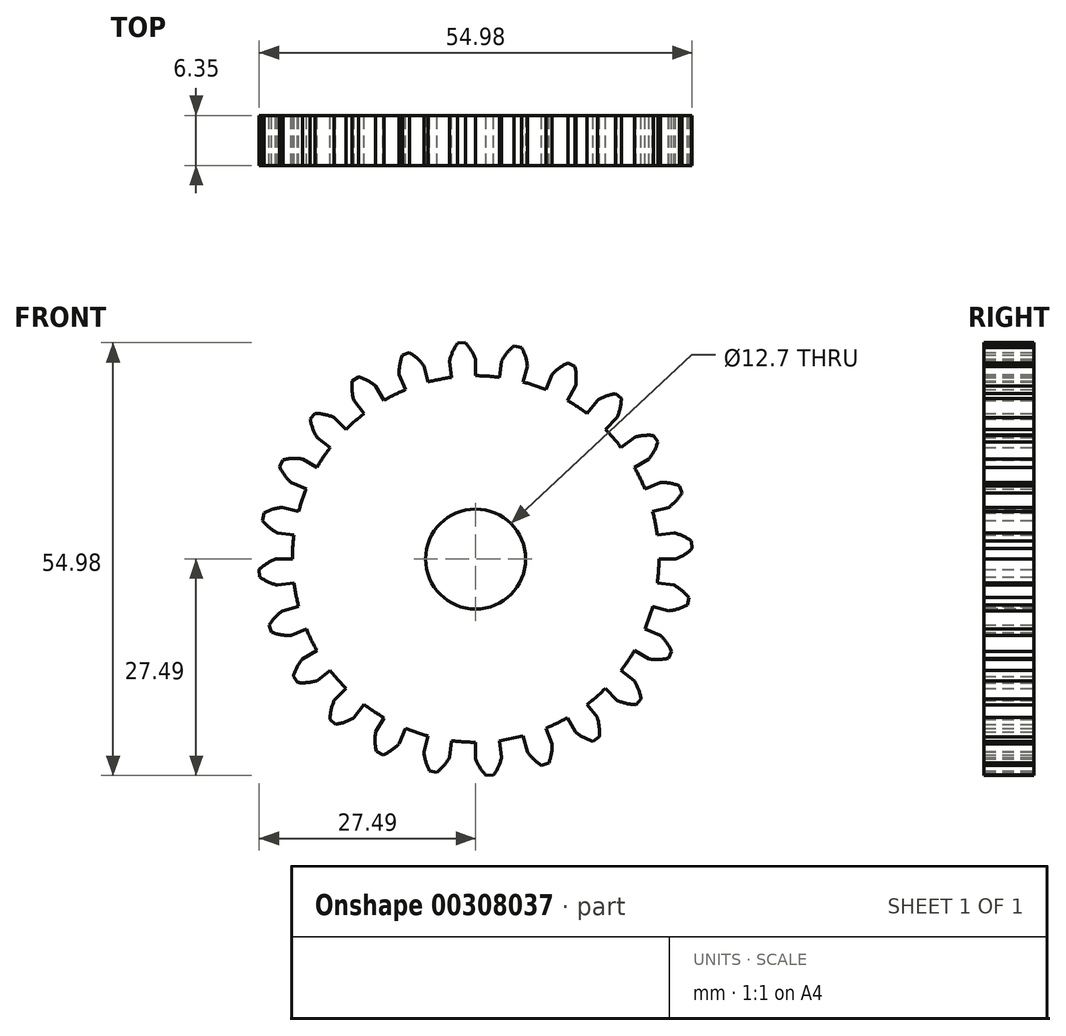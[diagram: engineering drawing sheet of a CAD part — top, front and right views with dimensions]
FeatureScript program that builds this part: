
annotation { "Feature Type Name" : "Feature", "Feature Type Description" : "" }
export const myFeature = defineFeature(function(context is Context, id is Id, definition is map)
    precondition{}
    {
        {
            var Q0;
            Q0=qCreatedBy(makeId("Front.planeOp"),FACE);
            var sketch = newSketch(context, id + "F0", { "sketchPlane" : qUnion([Q0])});
            skArc(sketch, "E0", {"start": v(-3.04, 23.08) * mm, "mid": v(-4.54, 22.83) * mm, "end": v(-6.03, 22.49) * mm});
            skLineSegment(sketch, "E1", {"start": v(0, 23.28) * mm, "end": v(0, 25.4) * mm});
            skArc(sketch, "E2.trimOffspring", {"start": v(0, 25.4) * mm, "mid": v(-0.56, 26.5) * mm, "end": v(-1.32, 27.49) * mm});
            skPoint(sketch, "E3.trimOffspring.end.orphan", {"position": v(0, 47.4) * mm});
            skLineSegment(sketch, "E4", {"start": v(-1.32, 27.49) * mm, "end": v(-1.8, 27.46) * mm});
            skLineSegment(sketch, "E5.MirrorCS", {"start": v(-2.28, 27.43) * mm, "end": v(-1.8, 27.46) * mm});
            skArc(sketch, "E6.MirrorCS", {"start": v(-3.32, 25.18) * mm, "mid": v(-2.9, 26.36) * mm, "end": v(-2.28, 27.43) * mm});
            skLineSegment(sketch, "E7.MirrorCS", {"start": v(-3.04, 23.08) * mm, "end": v(-3.32, 25.18) * mm});
            skLineSegment(sketch, "E8.1.0", {"start": v(-8.9, 21.5) * mm, "end": v(-9.72, 23.47) * mm});
            skArc(sketch, "E8.1.1", {"start": v(-9.72, 23.47) * mm, "mid": v(-9.63, 24.7) * mm, "end": v(-9.3, 25.9) * mm});
            skLineSegment(sketch, "E8.1.2", {"start": v(-9.3, 25.9) * mm, "end": v(-8.84, 26.06) * mm});
            skLineSegment(sketch, "E8.1.3", {"start": v(-8.39, 26.21) * mm, "end": v(-8.84, 26.06) * mm});
            skArc(sketch, "E8.1.4", {"start": v(-6.57, 24.53) * mm, "mid": v(-7.4, 25.46) * mm, "end": v(-8.39, 26.21) * mm});
            skLineSegment(sketch, "E8.1.5", {"start": v(-6.03, 22.49) * mm, "end": v(-6.57, 24.53) * mm});
            skLineSegment(sketch, "E8.2.0", {"start": v(-14.17, 18.47) * mm, "end": v(-15.46, 20.15) * mm});
            skArc(sketch, "E8.2.1", {"start": v(-15.46, 20.15) * mm, "mid": v(-15.7, 21.37) * mm, "end": v(-15.69, 22.61) * mm});
            skLineSegment(sketch, "E8.2.2", {"start": v(-15.69, 22.61) * mm, "end": v(-15.29, 22.88) * mm});
            skLineSegment(sketch, "E8.2.3", {"start": v(-14.89, 23.15) * mm, "end": v(-15.29, 22.88) * mm});
            skArc(sketch, "E8.2.4", {"start": v(-12.7, 22) * mm, "mid": v(-13.74, 22.68) * mm, "end": v(-14.89, 23.15) * mm});
            skLineSegment(sketch, "E8.2.5", {"start": v(-11.64, 20.16) * mm, "end": v(-12.7, 22) * mm});
            skLineSegment(sketch, "E8.3.0", {"start": v(-18.47, 14.17) * mm, "end": v(-20.15, 15.46) * mm});
            skArc(sketch, "E8.3.1", {"start": v(-20.15, 15.46) * mm, "mid": v(-20.7, 16.58) * mm, "end": v(-21, 17.78) * mm});
            skLineSegment(sketch, "E8.3.2", {"start": v(-21, 17.78) * mm, "end": v(-20.69, 18.14) * mm});
            skLineSegment(sketch, "E8.3.3", {"start": v(-20.37, 18.5) * mm, "end": v(-20.69, 18.14) * mm});
            skArc(sketch, "E8.3.4", {"start": v(-17.96, 17.96) * mm, "mid": v(-19.14, 18.35) * mm, "end": v(-20.37, 18.5) * mm});
            skLineSegment(sketch, "E8.3.5", {"start": v(-16.46, 16.46) * mm, "end": v(-17.96, 17.96) * mm});
            skLineSegment(sketch, "E8.4.0", {"start": v(-21.5, 8.9) * mm, "end": v(-23.47, 9.72) * mm});
            skArc(sketch, "E8.4.1", {"start": v(-23.47, 9.72) * mm, "mid": v(-24.28, 10.66) * mm, "end": v(-24.9, 11.74) * mm});
            skLineSegment(sketch, "E8.4.2", {"start": v(-24.9, 11.74) * mm, "end": v(-24.68, 12.17) * mm});
            skLineSegment(sketch, "E8.4.3", {"start": v(-24.47, 12.6) * mm, "end": v(-24.68, 12.17) * mm});
            skArc(sketch, "E8.4.4", {"start": v(-22, 12.7) * mm, "mid": v(-23.24, 12.77) * mm, "end": v(-24.47, 12.6) * mm});
            skLineSegment(sketch, "E8.4.5", {"start": v(-20.16, 11.64) * mm, "end": v(-22, 12.7) * mm});
            skLineSegment(sketch, "E8.5.0", {"start": v(-23.08, 3.04) * mm, "end": v(-25.18, 3.32) * mm});
            skArc(sketch, "E8.5.1", {"start": v(-25.18, 3.32) * mm, "mid": v(-26.2, 4.01) * mm, "end": v(-27.08, 4.9) * mm});
            skLineSegment(sketch, "E8.5.2", {"start": v(-27.08, 4.9) * mm, "end": v(-26.99, 5.37) * mm});
            skLineSegment(sketch, "E8.5.3", {"start": v(-26.9, 5.84) * mm, "end": v(-26.99, 5.37) * mm});
            skArc(sketch, "E8.5.4", {"start": v(-24.53, 6.57) * mm, "mid": v(-25.75, 6.32) * mm, "end": v(-26.9, 5.84) * mm});
            skLineSegment(sketch, "E8.5.5", {"start": v(-22.49, 6.03) * mm, "end": v(-24.53, 6.57) * mm});
            skLineSegment(sketch, "E8.6.0", {"start": v(-23.08, -3.04) * mm, "end": v(-25.18, -3.32) * mm});
            skArc(sketch, "E8.6.1", {"start": v(-25.18, -3.32) * mm, "mid": v(-26.36, -2.9) * mm, "end": v(-27.43, -2.28) * mm});
            skLineSegment(sketch, "E8.6.2", {"start": v(-27.43, -2.28) * mm, "end": v(-27.46, -1.8) * mm});
            skLineSegment(sketch, "E8.6.3", {"start": v(-27.49, -1.32) * mm, "end": v(-27.46, -1.8) * mm});
            skArc(sketch, "E8.6.4", {"start": v(-25.4, 0) * mm, "mid": v(-26.5, -0.56) * mm, "end": v(-27.49, -1.32) * mm});
            skLineSegment(sketch, "E8.6.5", {"start": v(-23.28, 0) * mm, "end": v(-25.4, 0) * mm});
            skLineSegment(sketch, "E8.7.0", {"start": v(-21.5, -8.9) * mm, "end": v(-23.47, -9.72) * mm});
            skArc(sketch, "E8.7.1", {"start": v(-23.47, -9.72) * mm, "mid": v(-24.7, -9.63) * mm, "end": v(-25.9, -9.3) * mm});
            skLineSegment(sketch, "E8.7.2", {"start": v(-25.9, -9.3) * mm, "end": v(-26.06, -8.84) * mm});
            skLineSegment(sketch, "E8.7.3", {"start": v(-26.21, -8.39) * mm, "end": v(-26.06, -8.84) * mm});
            skArc(sketch, "E8.7.4", {"start": v(-24.53, -6.57) * mm, "mid": v(-25.46, -7.4) * mm, "end": v(-26.21, -8.39) * mm});
            skLineSegment(sketch, "E8.7.5", {"start": v(-22.49, -6.03) * mm, "end": v(-24.53, -6.57) * mm});
            skLineSegment(sketch, "E8.8.0", {"start": v(-18.47, -14.17) * mm, "end": v(-20.15, -15.46) * mm});
            skArc(sketch, "E8.8.1", {"start": v(-20.15, -15.46) * mm, "mid": v(-21.37, -15.7) * mm, "end": v(-22.61, -15.69) * mm});
            skLineSegment(sketch, "E8.8.2", {"start": v(-22.61, -15.69) * mm, "end": v(-22.88, -15.29) * mm});
            skLineSegment(sketch, "E8.8.3", {"start": v(-23.15, -14.89) * mm, "end": v(-22.88, -15.29) * mm});
            skArc(sketch, "E8.8.4", {"start": v(-22, -12.7) * mm, "mid": v(-22.68, -13.74) * mm, "end": v(-23.15, -14.89) * mm});
            skLineSegment(sketch, "E8.8.5", {"start": v(-20.16, -11.64) * mm, "end": v(-22, -12.7) * mm});
            skLineSegment(sketch, "E8.9.0", {"start": v(-14.17, -18.47) * mm, "end": v(-15.46, -20.15) * mm});
            skArc(sketch, "E8.9.1", {"start": v(-15.46, -20.15) * mm, "mid": v(-16.58, -20.7) * mm, "end": v(-17.78, -21) * mm});
            skLineSegment(sketch, "E8.9.2", {"start": v(-17.78, -21) * mm, "end": v(-18.14, -20.69) * mm});
            skLineSegment(sketch, "E8.9.3", {"start": v(-18.5, -20.37) * mm, "end": v(-18.14, -20.69) * mm});
            skArc(sketch, "E8.9.4", {"start": v(-17.96, -17.96) * mm, "mid": v(-18.35, -19.14) * mm, "end": v(-18.5, -20.37) * mm});
            skLineSegment(sketch, "E8.9.5", {"start": v(-16.46, -16.46) * mm, "end": v(-17.96, -17.96) * mm});
            skLineSegment(sketch, "E8.10.0", {"start": v(-8.9, -21.5) * mm, "end": v(-9.72, -23.47) * mm});
            skArc(sketch, "E8.10.1", {"start": v(-9.72, -23.47) * mm, "mid": v(-10.66, -24.28) * mm, "end": v(-11.74, -24.9) * mm});
            skLineSegment(sketch, "E8.10.2", {"start": v(-11.74, -24.9) * mm, "end": v(-12.17, -24.68) * mm});
            skLineSegment(sketch, "E8.10.3", {"start": v(-12.6, -24.47) * mm, "end": v(-12.17, -24.68) * mm});
            skArc(sketch, "E8.10.4", {"start": v(-12.7, -22) * mm, "mid": v(-12.77, -23.24) * mm, "end": v(-12.6, -24.47) * mm});
            skLineSegment(sketch, "E8.10.5", {"start": v(-11.64, -20.16) * mm, "end": v(-12.7, -22) * mm});
            skLineSegment(sketch, "E8.11.0", {"start": v(-3.04, -23.08) * mm, "end": v(-3.32, -25.18) * mm});
            skArc(sketch, "E8.11.1", {"start": v(-3.32, -25.18) * mm, "mid": v(-4.01, -26.2) * mm, "end": v(-4.9, -27.08) * mm});
            skLineSegment(sketch, "E8.11.2", {"start": v(-4.9, -27.08) * mm, "end": v(-5.37, -26.99) * mm});
            skLineSegment(sketch, "E8.11.3", {"start": v(-5.84, -26.9) * mm, "end": v(-5.37, -26.99) * mm});
            skArc(sketch, "E8.11.4", {"start": v(-6.57, -24.53) * mm, "mid": v(-6.32, -25.75) * mm, "end": v(-5.84, -26.9) * mm});
            skLineSegment(sketch, "E8.11.5", {"start": v(-6.03, -22.49) * mm, "end": v(-6.57, -24.53) * mm});
            skLineSegment(sketch, "E8.12.0", {"start": v(3.04, -23.08) * mm, "end": v(3.32, -25.18) * mm});
            skArc(sketch, "E8.12.1", {"start": v(3.32, -25.18) * mm, "mid": v(2.9, -26.36) * mm, "end": v(2.28, -27.43) * mm});
            skLineSegment(sketch, "E8.12.2", {"start": v(2.28, -27.43) * mm, "end": v(1.8, -27.46) * mm});
            skLineSegment(sketch, "E8.12.3", {"start": v(1.32, -27.49) * mm, "end": v(1.8, -27.46) * mm});
            skArc(sketch, "E8.12.4", {"start": v(0, -25.4) * mm, "mid": v(0.56, -26.5) * mm, "end": v(1.32, -27.49) * mm});
            skLineSegment(sketch, "E8.12.5", {"start": v(0, -23.28) * mm, "end": v(0, -25.4) * mm});
            skLineSegment(sketch, "E8.13.0", {"start": v(8.9, -21.5) * mm, "end": v(9.72, -23.47) * mm});
            skArc(sketch, "E8.13.1", {"start": v(9.72, -23.47) * mm, "mid": v(9.63, -24.7) * mm, "end": v(9.3, -25.9) * mm});
            skLineSegment(sketch, "E8.13.2", {"start": v(9.3, -25.9) * mm, "end": v(8.84, -26.06) * mm});
            skLineSegment(sketch, "E8.13.3", {"start": v(8.39, -26.21) * mm, "end": v(8.84, -26.06) * mm});
            skArc(sketch, "E8.13.4", {"start": v(6.57, -24.53) * mm, "mid": v(7.4, -25.46) * mm, "end": v(8.39, -26.21) * mm});
            skLineSegment(sketch, "E8.13.5", {"start": v(6.03, -22.49) * mm, "end": v(6.57, -24.53) * mm});
            skLineSegment(sketch, "E8.14.0", {"start": v(14.17, -18.47) * mm, "end": v(15.46, -20.15) * mm});
            skArc(sketch, "E8.14.1", {"start": v(15.46, -20.15) * mm, "mid": v(15.7, -21.37) * mm, "end": v(15.69, -22.61) * mm});
            skLineSegment(sketch, "E8.14.2", {"start": v(15.69, -22.61) * mm, "end": v(15.29, -22.88) * mm});
            skLineSegment(sketch, "E8.14.3", {"start": v(14.89, -23.15) * mm, "end": v(15.29, -22.88) * mm});
            skArc(sketch, "E8.14.4", {"start": v(12.7, -22) * mm, "mid": v(13.74, -22.68) * mm, "end": v(14.89, -23.15) * mm});
            skLineSegment(sketch, "E8.14.5", {"start": v(11.64, -20.16) * mm, "end": v(12.7, -22) * mm});
            skLineSegment(sketch, "E8.15.0", {"start": v(18.47, -14.17) * mm, "end": v(20.15, -15.46) * mm});
            skArc(sketch, "E8.15.1", {"start": v(20.15, -15.46) * mm, "mid": v(20.7, -16.58) * mm, "end": v(21, -17.78) * mm});
            skLineSegment(sketch, "E8.15.2", {"start": v(21, -17.78) * mm, "end": v(20.69, -18.14) * mm});
            skLineSegment(sketch, "E8.15.3", {"start": v(20.37, -18.5) * mm, "end": v(20.69, -18.14) * mm});
            skArc(sketch, "E8.15.4", {"start": v(17.96, -17.96) * mm, "mid": v(19.14, -18.35) * mm, "end": v(20.37, -18.5) * mm});
            skLineSegment(sketch, "E8.15.5", {"start": v(16.46, -16.46) * mm, "end": v(17.96, -17.96) * mm});
            skLineSegment(sketch, "E8.16.0", {"start": v(21.5, -8.9) * mm, "end": v(23.47, -9.72) * mm});
            skArc(sketch, "E8.16.1", {"start": v(23.47, -9.72) * mm, "mid": v(24.28, -10.66) * mm, "end": v(24.9, -11.74) * mm});
            skLineSegment(sketch, "E8.16.2", {"start": v(24.9, -11.74) * mm, "end": v(24.68, -12.17) * mm});
            skLineSegment(sketch, "E8.16.3", {"start": v(24.47, -12.6) * mm, "end": v(24.68, -12.17) * mm});
            skArc(sketch, "E8.16.4", {"start": v(22, -12.7) * mm, "mid": v(23.24, -12.77) * mm, "end": v(24.47, -12.6) * mm});
            skLineSegment(sketch, "E8.16.5", {"start": v(20.16, -11.64) * mm, "end": v(22, -12.7) * mm});
            skLineSegment(sketch, "E8.17.0", {"start": v(23.08, -3.04) * mm, "end": v(25.18, -3.32) * mm});
            skArc(sketch, "E8.17.1", {"start": v(25.18, -3.32) * mm, "mid": v(26.2, -4.01) * mm, "end": v(27.08, -4.9) * mm});
            skLineSegment(sketch, "E8.17.2", {"start": v(27.08, -4.9) * mm, "end": v(26.99, -5.37) * mm});
            skLineSegment(sketch, "E8.17.3", {"start": v(26.9, -5.84) * mm, "end": v(26.99, -5.37) * mm});
            skArc(sketch, "E8.17.4", {"start": v(24.53, -6.57) * mm, "mid": v(25.75, -6.32) * mm, "end": v(26.9, -5.84) * mm});
            skLineSegment(sketch, "E8.17.5", {"start": v(22.49, -6.03) * mm, "end": v(24.53, -6.57) * mm});
            skLineSegment(sketch, "E8.18.0", {"start": v(23.08, 3.04) * mm, "end": v(25.18, 3.32) * mm});
            skArc(sketch, "E8.18.1", {"start": v(25.18, 3.32) * mm, "mid": v(26.36, 2.9) * mm, "end": v(27.43, 2.28) * mm});
            skLineSegment(sketch, "E8.18.2", {"start": v(27.43, 2.28) * mm, "end": v(27.46, 1.8) * mm});
            skLineSegment(sketch, "E8.18.3", {"start": v(27.49, 1.32) * mm, "end": v(27.46, 1.8) * mm});
            skArc(sketch, "E8.18.4", {"start": v(25.4, 0) * mm, "mid": v(26.5, 0.56) * mm, "end": v(27.49, 1.32) * mm});
            skLineSegment(sketch, "E8.18.5", {"start": v(23.28, 0) * mm, "end": v(25.4, 0) * mm});
            skLineSegment(sketch, "E8.19.0", {"start": v(21.5, 8.9) * mm, "end": v(23.47, 9.72) * mm});
            skArc(sketch, "E8.19.1", {"start": v(23.47, 9.72) * mm, "mid": v(24.7, 9.63) * mm, "end": v(25.9, 9.3) * mm});
            skLineSegment(sketch, "E8.19.2", {"start": v(25.9, 9.3) * mm, "end": v(26.06, 8.84) * mm});
            skLineSegment(sketch, "E8.19.3", {"start": v(26.21, 8.39) * mm, "end": v(26.06, 8.84) * mm});
            skArc(sketch, "E8.19.4", {"start": v(24.53, 6.57) * mm, "mid": v(25.46, 7.4) * mm, "end": v(26.21, 8.39) * mm});
            skLineSegment(sketch, "E8.19.5", {"start": v(22.49, 6.03) * mm, "end": v(24.53, 6.57) * mm});
            skLineSegment(sketch, "E8.20.0", {"start": v(18.47, 14.17) * mm, "end": v(20.15, 15.46) * mm});
            skArc(sketch, "E8.20.1", {"start": v(20.15, 15.46) * mm, "mid": v(21.37, 15.7) * mm, "end": v(22.61, 15.69) * mm});
            skLineSegment(sketch, "E8.20.2", {"start": v(22.61, 15.69) * mm, "end": v(22.88, 15.29) * mm});
            skLineSegment(sketch, "E8.20.3", {"start": v(23.15, 14.89) * mm, "end": v(22.88, 15.29) * mm});
            skArc(sketch, "E8.20.4", {"start": v(22, 12.7) * mm, "mid": v(22.68, 13.74) * mm, "end": v(23.15, 14.89) * mm});
            skLineSegment(sketch, "E8.20.5", {"start": v(20.16, 11.64) * mm, "end": v(22, 12.7) * mm});
            skLineSegment(sketch, "E8.21.0", {"start": v(14.17, 18.47) * mm, "end": v(15.46, 20.15) * mm});
            skArc(sketch, "E8.21.1", {"start": v(15.46, 20.15) * mm, "mid": v(16.58, 20.7) * mm, "end": v(17.78, 21) * mm});
            skLineSegment(sketch, "E8.21.2", {"start": v(17.78, 21) * mm, "end": v(18.14, 20.69) * mm});
            skLineSegment(sketch, "E8.21.3", {"start": v(18.5, 20.37) * mm, "end": v(18.14, 20.69) * mm});
            skArc(sketch, "E8.21.4", {"start": v(17.96, 17.96) * mm, "mid": v(18.35, 19.14) * mm, "end": v(18.5, 20.37) * mm});
            skLineSegment(sketch, "E8.21.5", {"start": v(16.46, 16.46) * mm, "end": v(17.96, 17.96) * mm});
            skLineSegment(sketch, "E8.22.0", {"start": v(8.9, 21.5) * mm, "end": v(9.72, 23.47) * mm});
            skArc(sketch, "E8.22.1", {"start": v(9.72, 23.47) * mm, "mid": v(10.66, 24.28) * mm, "end": v(11.74, 24.9) * mm});
            skLineSegment(sketch, "E8.22.2", {"start": v(11.74, 24.9) * mm, "end": v(12.17, 24.68) * mm});
            skLineSegment(sketch, "E8.22.3", {"start": v(12.6, 24.47) * mm, "end": v(12.17, 24.68) * mm});
            skArc(sketch, "E8.22.4", {"start": v(12.7, 22) * mm, "mid": v(12.77, 23.24) * mm, "end": v(12.6, 24.47) * mm});
            skLineSegment(sketch, "E8.22.5", {"start": v(11.64, 20.16) * mm, "end": v(12.7, 22) * mm});
            skLineSegment(sketch, "E8.23.0", {"start": v(3.04, 23.08) * mm, "end": v(3.32, 25.18) * mm});
            skArc(sketch, "E8.23.1", {"start": v(3.32, 25.18) * mm, "mid": v(4.01, 26.2) * mm, "end": v(4.9, 27.08) * mm});
            skLineSegment(sketch, "E8.23.2", {"start": v(4.9, 27.08) * mm, "end": v(5.37, 26.99) * mm});
            skLineSegment(sketch, "E8.23.3", {"start": v(5.84, 26.9) * mm, "end": v(5.37, 26.99) * mm});
            skArc(sketch, "E8.23.4", {"start": v(6.57, 24.53) * mm, "mid": v(6.32, 25.75) * mm, "end": v(5.84, 26.9) * mm});
            skLineSegment(sketch, "E8.23.5", {"start": v(6.03, 22.49) * mm, "end": v(6.57, 24.53) * mm});
            skArc(sketch, "E9.trimOffspring", {"start": v(3.04, 23.08) * mm, "mid": v(1.52, 23.23) * mm, "end": v(0, 23.28) * mm});
            skArc(sketch, "E10.trimOffspring", {"start": v(-8.9, 21.5) * mm, "mid": v(-10.3, 20.88) * mm, "end": v(-11.64, 20.16) * mm});
            skArc(sketch, "E11.trimOffspring", {"start": v(8.9, 21.5) * mm, "mid": v(7.48, 22.04) * mm, "end": v(6.03, 22.49) * mm});
            skArc(sketch, "E12.trimOffspring", {"start": v(-14.17, 18.47) * mm, "mid": v(-15.35, 17.5) * mm, "end": v(-16.46, 16.46) * mm});
            skArc(sketch, "E13.trimOffspring", {"start": v(14.17, 18.47) * mm, "mid": v(12.93, 19.36) * mm, "end": v(11.64, 20.16) * mm});
            skArc(sketch, "E14.trimOffspring", {"start": v(-18.47, 14.17) * mm, "mid": v(-19.36, 12.93) * mm, "end": v(-20.16, 11.64) * mm});
            skArc(sketch, "E15.trimOffspring", {"start": v(18.47, 14.17) * mm, "mid": v(17.5, 15.35) * mm, "end": v(16.46, 16.46) * mm});
            skArc(sketch, "E16.trimOffspring", {"start": v(-21.5, 8.9) * mm, "mid": v(-22.04, 7.48) * mm, "end": v(-22.49, 6.03) * mm});
            skArc(sketch, "E17.trimOffspring", {"start": v(21.5, 8.9) * mm, "mid": v(20.88, 10.3) * mm, "end": v(20.16, 11.64) * mm});
            skArc(sketch, "E18.trimOffspring", {"start": v(-23.08, 3.04) * mm, "mid": v(-23.23, 1.52) * mm, "end": v(-23.28, 0) * mm});
            skArc(sketch, "E19.trimOffspring", {"start": v(23.08, 3.04) * mm, "mid": v(22.83, 4.54) * mm, "end": v(22.49, 6.03) * mm});
            skArc(sketch, "E20.trimOffspring", {"start": v(-23.08, -3.04) * mm, "mid": v(-22.83, -4.54) * mm, "end": v(-22.49, -6.03) * mm});
            skArc(sketch, "E21.trimOffspring", {"start": v(23.08, -3.04) * mm, "mid": v(23.23, -1.52) * mm, "end": v(23.28, 0) * mm});
            skArc(sketch, "E22.trimOffspring", {"start": v(-21.5, -8.9) * mm, "mid": v(-20.88, -10.3) * mm, "end": v(-20.16, -11.64) * mm});
            skArc(sketch, "E23.trimOffspring", {"start": v(21.5, -8.9) * mm, "mid": v(22.04, -7.48) * mm, "end": v(22.49, -6.03) * mm});
            skArc(sketch, "E24.trimOffspring", {"start": v(-18.47, -14.17) * mm, "mid": v(-17.5, -15.35) * mm, "end": v(-16.46, -16.46) * mm});
            skArc(sketch, "E25.trimOffspring", {"start": v(-14.17, -18.47) * mm, "mid": v(-12.93, -19.36) * mm, "end": v(-11.64, -20.16) * mm});
            skArc(sketch, "E26.trimOffspring", {"start": v(-8.9, -21.5) * mm, "mid": v(-7.48, -22.04) * mm, "end": v(-6.03, -22.49) * mm});
            skArc(sketch, "E27.trimOffspring", {"start": v(-3.04, -23.08) * mm, "mid": v(-1.52, -23.23) * mm, "end": v(0, -23.28) * mm});
            skArc(sketch, "E28.trimOffspring", {"start": v(8.9, -21.5) * mm, "mid": v(10.3, -20.88) * mm, "end": v(11.64, -20.16) * mm});
            skArc(sketch, "E29.trimOffspring", {"start": v(18.47, -14.17) * mm, "mid": v(19.36, -12.93) * mm, "end": v(20.16, -11.64) * mm});
            skLineSegment(sketch, "E30", {"start": v(3.04, -23.08) * mm, "end": v(6.03, -22.49) * mm});
            skArc(sketch, "E31.trimOffspring", {"start": v(14.17, -18.47) * mm, "mid": v(15.35, -17.5) * mm, "end": v(16.46, -16.46) * mm});
            skSolve(sketch);
        }
        {
            var Q0;
            Q0=makeQuery(id+"F0.imprint","IMPRINT",FACE,{"disambiguationData":[TD([[makeQuery(id+"F0.imprint","IMPRINT",EDGE,{"derivedFrom":sQuery(id+"F0.wireOp",EDGE,"E0")}),1.0]])]});
            extrude(context, id + "F1", {"entities" : qUnion([Q0]), "depth" : 6.35 * mm});
        }
        {
            var Q0;
            Q0=makeQuery(id+"F1.opExtrude","CAP_FACE",FACE,{"disambiguationData":[OSD([sQuery(id+"F0.wireOp",EDGE,"E0"),sQuery(id+"F0.wireOp",EDGE,"E1"),sQuery(id+"F0.wireOp",EDGE,"E2.trimOffspring"),sQuery(id+"F0.wireOp",EDGE,"E4"),sQuery(id+"F0.wireOp",EDGE,"E5.MirrorCS"),sQuery(id+"F0.wireOp",EDGE,"E6.MirrorCS"),sQuery(id+"F0.wireOp",EDGE,"E7.MirrorCS"),sQuery(id+"F0.wireOp",EDGE,"E8.1.0"),sQuery(id+"F0.wireOp",EDGE,"E8.1.1"),sQuery(id+"F0.wireOp",EDGE,"E8.1.2"),sQuery(id+"F0.wireOp",EDGE,"E8.1.3"),sQuery(id+"F0.wireOp",EDGE,"E8.1.4"),sQuery(id+"F0.wireOp",EDGE,"E8.1.5"),sQuery(id+"F0.wireOp",EDGE,"E8.2.0"),sQuery(id+"F0.wireOp",EDGE,"E8.2.1"),sQuery(id+"F0.wireOp",EDGE,"E8.2.2"),sQuery(id+"F0.wireOp",EDGE,"E8.2.3"),sQuery(id+"F0.wireOp",EDGE,"E8.2.4"),sQuery(id+"F0.wireOp",EDGE,"E8.2.5"),sQuery(id+"F0.wireOp",EDGE,"E8.3.0"),sQuery(id+"F0.wireOp",EDGE,"E8.3.1"),sQuery(id+"F0.wireOp",EDGE,"E8.3.2"),sQuery(id+"F0.wireOp",EDGE,"E8.3.3"),sQuery(id+"F0.wireOp",EDGE,"E8.3.4"),sQuery(id+"F0.wireOp",EDGE,"E8.3.5"),sQuery(id+"F0.wireOp",EDGE,"E8.4.0"),sQuery(id+"F0.wireOp",EDGE,"E8.4.1"),sQuery(id+"F0.wireOp",EDGE,"E8.4.2"),sQuery(id+"F0.wireOp",EDGE,"E8.4.3"),sQuery(id+"F0.wireOp",EDGE,"E8.4.4"),sQuery(id+"F0.wireOp",EDGE,"E8.4.5"),sQuery(id+"F0.wireOp",EDGE,"E8.5.0"),sQuery(id+"F0.wireOp",EDGE,"E8.5.1"),sQuery(id+"F0.wireOp",EDGE,"E8.5.2"),sQuery(id+"F0.wireOp",EDGE,"E8.5.3"),sQuery(id+"F0.wireOp",EDGE,"E8.5.4"),sQuery(id+"F0.wireOp",EDGE,"E8.5.5"),sQuery(id+"F0.wireOp",EDGE,"E8.6.0"),sQuery(id+"F0.wireOp",EDGE,"E8.6.1"),sQuery(id+"F0.wireOp",EDGE,"E8.6.2"),sQuery(id+"F0.wireOp",EDGE,"E8.6.3"),sQuery(id+"F0.wireOp",EDGE,"E8.6.4"),sQuery(id+"F0.wireOp",EDGE,"E8.6.5"),sQuery(id+"F0.wireOp",EDGE,"E8.7.0"),sQuery(id+"F0.wireOp",EDGE,"E8.7.1"),sQuery(id+"F0.wireOp",EDGE,"E8.7.2"),sQuery(id+"F0.wireOp",EDGE,"E8.7.3"),sQuery(id+"F0.wireOp",EDGE,"E8.7.4"),sQuery(id+"F0.wireOp",EDGE,"E8.7.5"),sQuery(id+"F0.wireOp",EDGE,"E8.8.0"),sQuery(id+"F0.wireOp",EDGE,"E8.8.1"),sQuery(id+"F0.wireOp",EDGE,"E8.8.2"),sQuery(id+"F0.wireOp",EDGE,"E8.8.3"),sQuery(id+"F0.wireOp",EDGE,"E8.8.4"),sQuery(id+"F0.wireOp",EDGE,"E8.8.5"),sQuery(id+"F0.wireOp",EDGE,"E8.9.0"),sQuery(id+"F0.wireOp",EDGE,"E8.9.1"),sQuery(id+"F0.wireOp",EDGE,"E8.9.2"),sQuery(id+"F0.wireOp",EDGE,"E8.9.3"),sQuery(id+"F0.wireOp",EDGE,"E8.9.4"),sQuery(id+"F0.wireOp",EDGE,"E8.9.5"),sQuery(id+"F0.wireOp",EDGE,"E8.10.0"),sQuery(id+"F0.wireOp",EDGE,"E8.10.1"),sQuery(id+"F0.wireOp",EDGE,"E8.10.2"),sQuery(id+"F0.wireOp",EDGE,"E8.10.3"),sQuery(id+"F0.wireOp",EDGE,"E8.10.4"),sQuery(id+"F0.wireOp",EDGE,"E8.10.5"),sQuery(id+"F0.wireOp",EDGE,"E8.11.0"),sQuery(id+"F0.wireOp",EDGE,"E8.11.1"),sQuery(id+"F0.wireOp",EDGE,"E8.11.2"),sQuery(id+"F0.wireOp",EDGE,"E8.11.3"),sQuery(id+"F0.wireOp",EDGE,"E8.11.4"),sQuery(id+"F0.wireOp",EDGE,"E8.11.5"),sQuery(id+"F0.wireOp",EDGE,"E8.12.0"),sQuery(id+"F0.wireOp",EDGE,"E8.12.1"),sQuery(id+"F0.wireOp",EDGE,"E8.12.2"),sQuery(id+"F0.wireOp",EDGE,"E8.12.3"),sQuery(id+"F0.wireOp",EDGE,"E8.12.4"),sQuery(id+"F0.wireOp",EDGE,"E8.12.5"),sQuery(id+"F0.wireOp",EDGE,"E8.13.0"),sQuery(id+"F0.wireOp",EDGE,"E8.13.1"),sQuery(id+"F0.wireOp",EDGE,"E8.13.2"),sQuery(id+"F0.wireOp",EDGE,"E8.13.3"),sQuery(id+"F0.wireOp",EDGE,"E8.13.4"),sQuery(id+"F0.wireOp",EDGE,"E8.13.5"),sQuery(id+"F0.wireOp",EDGE,"E8.14.0"),sQuery(id+"F0.wireOp",EDGE,"E8.14.1"),sQuery(id+"F0.wireOp",EDGE,"E8.14.2"),sQuery(id+"F0.wireOp",EDGE,"E8.14.3"),sQuery(id+"F0.wireOp",EDGE,"E8.14.4"),sQuery(id+"F0.wireOp",EDGE,"E8.14.5"),sQuery(id+"F0.wireOp",EDGE,"E8.15.0"),sQuery(id+"F0.wireOp",EDGE,"E8.15.1"),sQuery(id+"F0.wireOp",EDGE,"E8.15.2"),sQuery(id+"F0.wireOp",EDGE,"E8.15.3"),sQuery(id+"F0.wireOp",EDGE,"E8.15.4"),sQuery(id+"F0.wireOp",EDGE,"E8.15.5"),sQuery(id+"F0.wireOp",EDGE,"E8.16.0"),sQuery(id+"F0.wireOp",EDGE,"E8.16.1"),sQuery(id+"F0.wireOp",EDGE,"E8.16.2"),sQuery(id+"F0.wireOp",EDGE,"E8.16.3"),sQuery(id+"F0.wireOp",EDGE,"E8.16.4"),sQuery(id+"F0.wireOp",EDGE,"E8.16.5"),sQuery(id+"F0.wireOp",EDGE,"E8.17.0"),sQuery(id+"F0.wireOp",EDGE,"E8.17.1"),sQuery(id+"F0.wireOp",EDGE,"E8.17.2"),sQuery(id+"F0.wireOp",EDGE,"E8.17.3"),sQuery(id+"F0.wireOp",EDGE,"E8.17.4"),sQuery(id+"F0.wireOp",EDGE,"E8.17.5"),sQuery(id+"F0.wireOp",EDGE,"E8.18.0"),sQuery(id+"F0.wireOp",EDGE,"E8.18.1"),sQuery(id+"F0.wireOp",EDGE,"E8.18.2"),sQuery(id+"F0.wireOp",EDGE,"E8.18.3"),sQuery(id+"F0.wireOp",EDGE,"E8.18.4"),sQuery(id+"F0.wireOp",EDGE,"E8.18.5"),sQuery(id+"F0.wireOp",EDGE,"E8.19.0"),sQuery(id+"F0.wireOp",EDGE,"E8.19.1"),sQuery(id+"F0.wireOp",EDGE,"E8.19.2"),sQuery(id+"F0.wireOp",EDGE,"E8.19.3"),sQuery(id+"F0.wireOp",EDGE,"E8.19.4"),sQuery(id+"F0.wireOp",EDGE,"E8.19.5"),sQuery(id+"F0.wireOp",EDGE,"E8.20.0"),sQuery(id+"F0.wireOp",EDGE,"E8.20.1"),sQuery(id+"F0.wireOp",EDGE,"E8.20.2"),sQuery(id+"F0.wireOp",EDGE,"E8.20.3"),sQuery(id+"F0.wireOp",EDGE,"E8.20.4"),sQuery(id+"F0.wireOp",EDGE,"E8.20.5"),sQuery(id+"F0.wireOp",EDGE,"E8.21.0"),sQuery(id+"F0.wireOp",EDGE,"E8.21.1"),sQuery(id+"F0.wireOp",EDGE,"E8.21.2"),sQuery(id+"F0.wireOp",EDGE,"E8.21.3"),sQuery(id+"F0.wireOp",EDGE,"E8.21.4"),sQuery(id+"F0.wireOp",EDGE,"E8.21.5"),sQuery(id+"F0.wireOp",EDGE,"E8.22.0"),sQuery(id+"F0.wireOp",EDGE,"E8.22.1"),sQuery(id+"F0.wireOp",EDGE,"E8.22.2"),sQuery(id+"F0.wireOp",EDGE,"E8.22.3"),sQuery(id+"F0.wireOp",EDGE,"E8.22.4"),sQuery(id+"F0.wireOp",EDGE,"E8.22.5"),sQuery(id+"F0.wireOp",EDGE,"E8.23.0"),sQuery(id+"F0.wireOp",EDGE,"E8.23.1"),sQuery(id+"F0.wireOp",EDGE,"E8.23.2"),sQuery(id+"F0.wireOp",EDGE,"E8.23.3"),sQuery(id+"F0.wireOp",EDGE,"E8.23.4"),sQuery(id+"F0.wireOp",EDGE,"E8.23.5"),sQuery(id+"F0.wireOp",EDGE,"E9.trimOffspring"),sQuery(id+"F0.wireOp",EDGE,"E10.trimOffspring"),sQuery(id+"F0.wireOp",EDGE,"E11.trimOffspring"),sQuery(id+"F0.wireOp",EDGE,"E12.trimOffspring"),sQuery(id+"F0.wireOp",EDGE,"E13.trimOffspring"),sQuery(id+"F0.wireOp",EDGE,"E14.trimOffspring"),sQuery(id+"F0.wireOp",EDGE,"E15.trimOffspring"),sQuery(id+"F0.wireOp",EDGE,"E16.trimOffspring"),sQuery(id+"F0.wireOp",EDGE,"E17.trimOffspring"),sQuery(id+"F0.wireOp",EDGE,"E18.trimOffspring"),sQuery(id+"F0.wireOp",EDGE,"E19.trimOffspring"),sQuery(id+"F0.wireOp",EDGE,"E20.trimOffspring"),sQuery(id+"F0.wireOp",EDGE,"E21.trimOffspring"),sQuery(id+"F0.wireOp",EDGE,"E22.trimOffspring"),sQuery(id+"F0.wireOp",EDGE,"E23.trimOffspring"),sQuery(id+"F0.wireOp",EDGE,"E24.trimOffspring"),sQuery(id+"F0.wireOp",EDGE,"E25.trimOffspring"),sQuery(id+"F0.wireOp",EDGE,"E26.trimOffspring"),sQuery(id+"F0.wireOp",EDGE,"E27.trimOffspring"),sQuery(id+"F0.wireOp",EDGE,"E28.trimOffspring"),sQuery(id+"F0.wireOp",EDGE,"E29.trimOffspring"),sQuery(id+"F0.wireOp",EDGE,"E30"),sQuery(id+"F0.wireOp",EDGE,"E31.trimOffspring")])],"isStart":false});
            var sketch = newSketch(context, id + "F2", { "sketchPlane" : qUnion([Q0])});
            skCircle(sketch, "E32", {"center": v(0, 0) * mm, "radius": 6.35 * mm});
            skSolve(sketch);
        }
        {
            var Q0;
            Q0=makeQuery(id+"F2.imprint","IMPRINT",FACE,{"disambiguationData":[TD([[makeQuery(id+"F2.imprint","IMPRINT",EDGE,{"derivedFrom":sQuery(id+"F2.wireOp",EDGE,"E32")}),1.0]])]});
            extrude(context, id + "F3", {"entities" : qUnion([Q0]), "operationType" : NewBodyOperationType.REMOVE, "endBound" : BoundingType.THROUGH_ALL, "oppositeDirection" : true, "depth" : 25.4 * mm});
        }
    });
